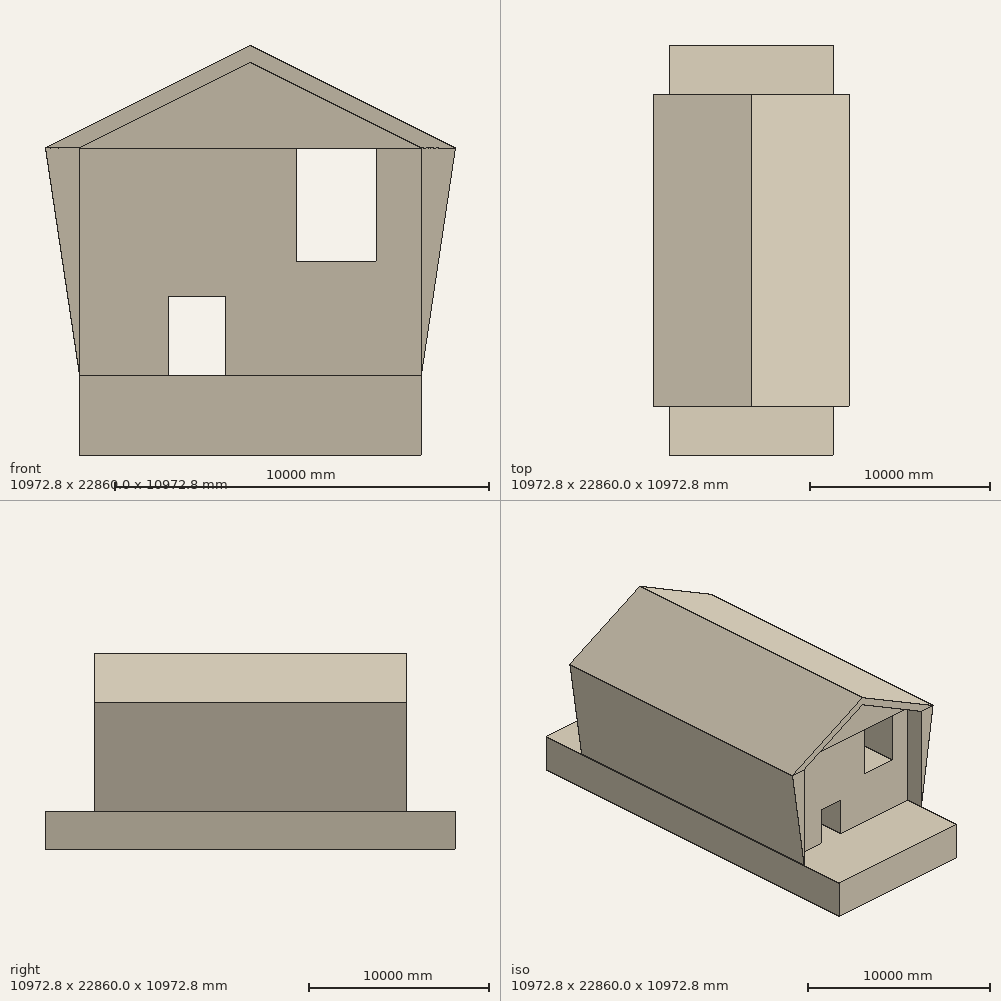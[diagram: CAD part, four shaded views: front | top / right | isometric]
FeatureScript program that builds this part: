
annotation { "Feature Type Name" : "Feature", "Feature Type Description" : "" }
export const myFeature = defineFeature(function(context is Context, id is Id, definition is map)
    precondition{}
    {
        {
            var Q0;
            Q0=qCreatedBy(makeId("Front.planeOp"),FACE);
            var sketch = newSketch(context, id + "F0", { "sketchPlane" : qUnion([Q0])});
            skLineSegment(sketch, "E0", {"start": v(0, 0) * mm, "end": v(-4572, 0) * mm});
            skLineSegment(sketch, "E1", {"start": v(0, 0) * mm, "end": v(4572, 0) * mm});
            skLineSegment(sketch, "E2", {"start": v(0, 0) * mm, "end": v(0, 2286) * mm});
            skLineSegment(sketch, "E3", {"start": v(0, 2286) * mm, "end": v(-4572, 0) * mm});
            skLineSegment(sketch, "E4", {"start": v(0, 2286) * mm, "end": v(4572, 0) * mm});
            skLineSegment(sketch, "E5", {"start": v(0, 2286) * mm, "end": v(0, 2743.2) * mm});
            skLineSegment(sketch, "E6", {"start": v(-4572, 0) * mm, "end": v(-5486.4, 0) * mm});
            skLineSegment(sketch, "E7", {"start": v(4572, 0) * mm, "end": v(5486.4, 0) * mm});
            skLineSegment(sketch, "E8", {"start": v(0, 2743.2) * mm, "end": v(-5486.4, 0) * mm});
            skLineSegment(sketch, "E9", {"start": v(0, 2743.2) * mm, "end": v(5486.4, 0) * mm});
            skLineSegment(sketch, "E10", {"start": v(-4572, 0) * mm, "end": v(-4572, -6096) * mm});
            skLineSegment(sketch, "E11", {"start": v(4572, 0) * mm, "end": v(4572, -6096) * mm});
            skLineSegment(sketch, "E12", {"start": v(4572, -6096) * mm, "end": v(-4572, -6096) * mm});
            skLineSegment(sketch, "E13", {"start": v(4572, -6096) * mm, "end": v(4572, -8229.6) * mm});
            skLineSegment(sketch, "E14", {"start": v(-4572, -6096) * mm, "end": v(-4572, -8229.6) * mm});
            skLineSegment(sketch, "E15", {"start": v(-4572, -8229.6) * mm, "end": v(4572, -8229.6) * mm});
            skLineSegment(sketch, "E16", {"start": v(-5486.4, 0) * mm, "end": v(-4572, -6096) * mm});
            skLineSegment(sketch, "E17", {"start": v(5486.4, 0) * mm, "end": v(4572, -6096) * mm});
            skLineSegment(sketch, "E18", {"start": v(-2187.34, -6096) * mm, "end": v(-2187.34, -3962.4) * mm});
            skLineSegment(sketch, "E19", {"start": v(-2187.34, -3962.4) * mm, "end": v(-663.34, -3962.4) * mm});
            skLineSegment(sketch, "E20", {"start": v(-663.34, -3962.4) * mm, "end": v(-663.34, -6096) * mm});
            skLineSegment(sketch, "E21", {"start": v(1234.44, 0) * mm, "end": v(1234.44, -3048) * mm});
            skLineSegment(sketch, "E22", {"start": v(1234.44, -3048) * mm, "end": v(3368.04, -3048) * mm});
            skLineSegment(sketch, "E23", {"start": v(3368.04, -3048) * mm, "end": v(3368.04, 0) * mm});
            skText(sketch, "E24", { "text": "Sebastian\n", "fontName": "OpenSans-Regular.ttf"});
            const initialGuessF0  = {"E24": [2.98025, 2.80847, 1, 0, 0.55002]};
            skSetInitialGuess(sketch, initialGuessF0);
            skSolve(sketch);
        }
        {
            var Q0;
            {var subQ0=sQuery(id+"F0.wireOp",EDGE,"E13");Q0=makeQuery(id+"F0.imprint","IMPRINT",FACE,{"disambiguationData":[TD([[makeQuery(id+"F0.imprint","IMPRINT",EDGE,{"derivedFrom":subQ0}),-1.0]])]});}
            extrude(context, id + "F1", {"entities" : qUnion([Q0]), "endBound" : BoundingType.SYMMETRIC, "depth" : 22860 * mm, "offsetDistance" : 30.48 * mm});
        }
        {
            var Q0;
            Q0=makeQuery(id+"F0.imprint","IMPRINT",FACE,{"disambiguationData":[TD([[makeQuery(id+"F0.imprint","IMPRINT",EDGE,{"derivedFrom":sQuery(id+"F0.wireOp",EDGE,"E3")}),-1.0]])]});
            var Q1;
            Q1=makeQuery(id+"F0.imprint","IMPRINT",FACE,{"disambiguationData":[TD([[makeQuery(id+"F0.imprint","IMPRINT",EDGE,{"derivedFrom":sQuery(id+"F0.wireOp",EDGE,"E4")}),1.0]])]});
            extrude(context, id + "F2", {"entities" : qUnion([Q0, Q1]), "endBound" : BoundingType.SYMMETRIC, "depth" : 17373.6 * mm, "offsetDistance" : 30.48 * mm});
        }
        {
            var Q0;
            Q0=makeQuery(id+"F0.imprint","IMPRINT",FACE,{"disambiguationData":[TD([[makeQuery(id+"F0.imprint","IMPRINT",EDGE,{"derivedFrom":sQuery(id+"F0.wireOp",EDGE,"E0")}),-1.0]])]});
            var Q1;
            {var subQ0=sQuery(id+"F0.wireOp",EDGE,"E2");Q1=makeQuery(id+"F0.imprint","IMPRINT",FACE,{"disambiguationData":[TD([[makeQuery(id+"F0.imprint","IMPRINT",EDGE,{"derivedFrom":subQ0}),-1.0]])]});}
            extrude(context, id + "F3", {"entities" : qUnion([Q0, Q1]), "operationType" : NewBodyOperationType.ADD, "endBound" : BoundingType.SYMMETRIC, "depth" : 15849.6 * mm, "offsetDistance" : 30.48 * mm});
        }
        {
            var Q0;
            {var subQ5=sQuery(id+"F0.wireOp",EDGE,"E0");Q0=makeQuery(id+"F0.imprint","IMPRINT",FACE,{"disambiguationData":[TD([[makeQuery(id+"F0.imprint","IMPRINT",EDGE,{"derivedFrom":subQ5}),1.0]])]});}
            extrude(context, id + "F4", {"entities" : qUnion([Q0]), "endBound" : BoundingType.SYMMETRIC, "depth" : 15240 * mm, "offsetDistance" : 30.48 * mm});
        }
        {
            var Q0;
            Q0=makeQuery(id+"F0.imprint","IMPRINT",FACE,{"disambiguationData":[TD([[makeQuery(id+"F0.imprint","IMPRINT",EDGE,{"derivedFrom":sQuery(id+"F0.wireOp",EDGE,"E6")}),1.0]])]});
            var Q1;
            Q1=makeQuery(id+"F0.imprint","IMPRINT",FACE,{"disambiguationData":[TD([[makeQuery(id+"F0.imprint","IMPRINT",EDGE,{"derivedFrom":sQuery(id+"F0.wireOp",EDGE,"E7")}),-1.0]])]});
            extrude(context, id + "F5", {"entities" : qUnion([Q0, Q1]), "endBound" : BoundingType.SYMMETRIC, "depth" : 17373.6 * mm, "offsetDistance" : 30.48 * mm});
        }
    });
